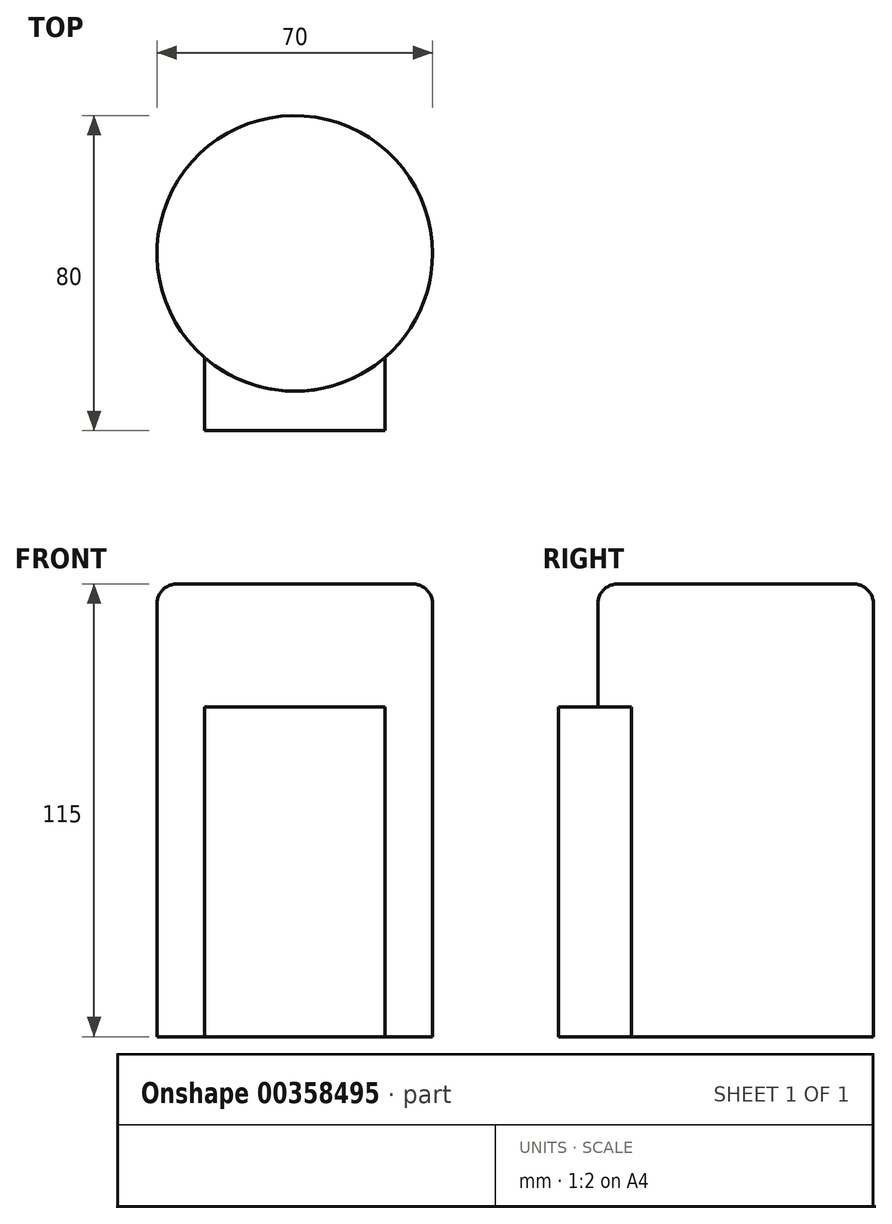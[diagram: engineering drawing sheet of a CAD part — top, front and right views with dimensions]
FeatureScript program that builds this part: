
annotation { "Feature Type Name" : "Feature", "Feature Type Description" : "" }
export const myFeature = defineFeature(function(context is Context, id is Id, definition is map)
    precondition{}
    {
        {
            var Q0;
            Q0=qCreatedBy(makeId("Top.planeOp"),FACE);
            var sketch = newSketch(context, id + "F0", { "sketchPlane" : qUnion([Q0])});
            skCircle(sketch, "E0", {"center": v(0, 0) * mm, "radius": 35 * mm});
            skSolve(sketch);
        }
        {
            var Q0;
            Q0 = qSketchRegion(id + "F0", true);
            extrude(context, id + "F1", {"entities" : qUnion([Q0]), "depth" : 115 * mm});
        }
        {
            var Q0;
            Q0=makeQuery(id+"F1.opExtrude","CAP_EDGE",EDGE,{"disambiguationData":[OSD([sQuery(id+"F0.wireOp",EDGE,"E0")])],"isStart":false});
            fillet(context, id + "F2", {"entities" : qUnion([Q0]), "radius" : 5 * mm, "tangentPropagation" : true, "allowEdgeOverflow" : false});
        }
        {
            var Q0;
            Q0=qCreatedBy(makeId("Front.planeOp"),FACE);
            var sketch = newSketch(context, id + "F3", { "sketchPlane" : qUnion([Q0])});
            skLineSegment(sketch, "E1.top", {"start": v(-22.9, 83.78) * mm, "end": v(22.9, 83.78) * mm});
            skLineSegment(sketch, "E1.left", {"start": v(-22.9, 28.15) * mm, "end": v(-22.9, 83.78) * mm});
            skLineSegment(sketch, "E1.right", {"start": v(22.9, 28.15) * mm, "end": v(22.9, 83.78) * mm});
            skPoint(sketch, "E1.middle", {"position": v(0, 55.97) * mm});
            skLineSegment(sketch, "E2.top", {"start": v(-22.9, 0) * mm, "end": v(22.9, 0) * mm});
            skLineSegment(sketch, "E2.left", {"start": v(-22.9, 28.15) * mm, "end": v(-22.9, 0) * mm});
            skLineSegment(sketch, "E2.right", {"start": v(22.9, 28.15) * mm, "end": v(22.9, 0) * mm});
            skSolve(sketch);
        }
        {
            var Q0;
            Q0 = qSketchRegion(id + "F3", true);
            extrude(context, id + "F4", {"entities" : qUnion([Q0]), "operationType" : NewBodyOperationType.ADD, "depth" : 45 * mm});
        }
    });
